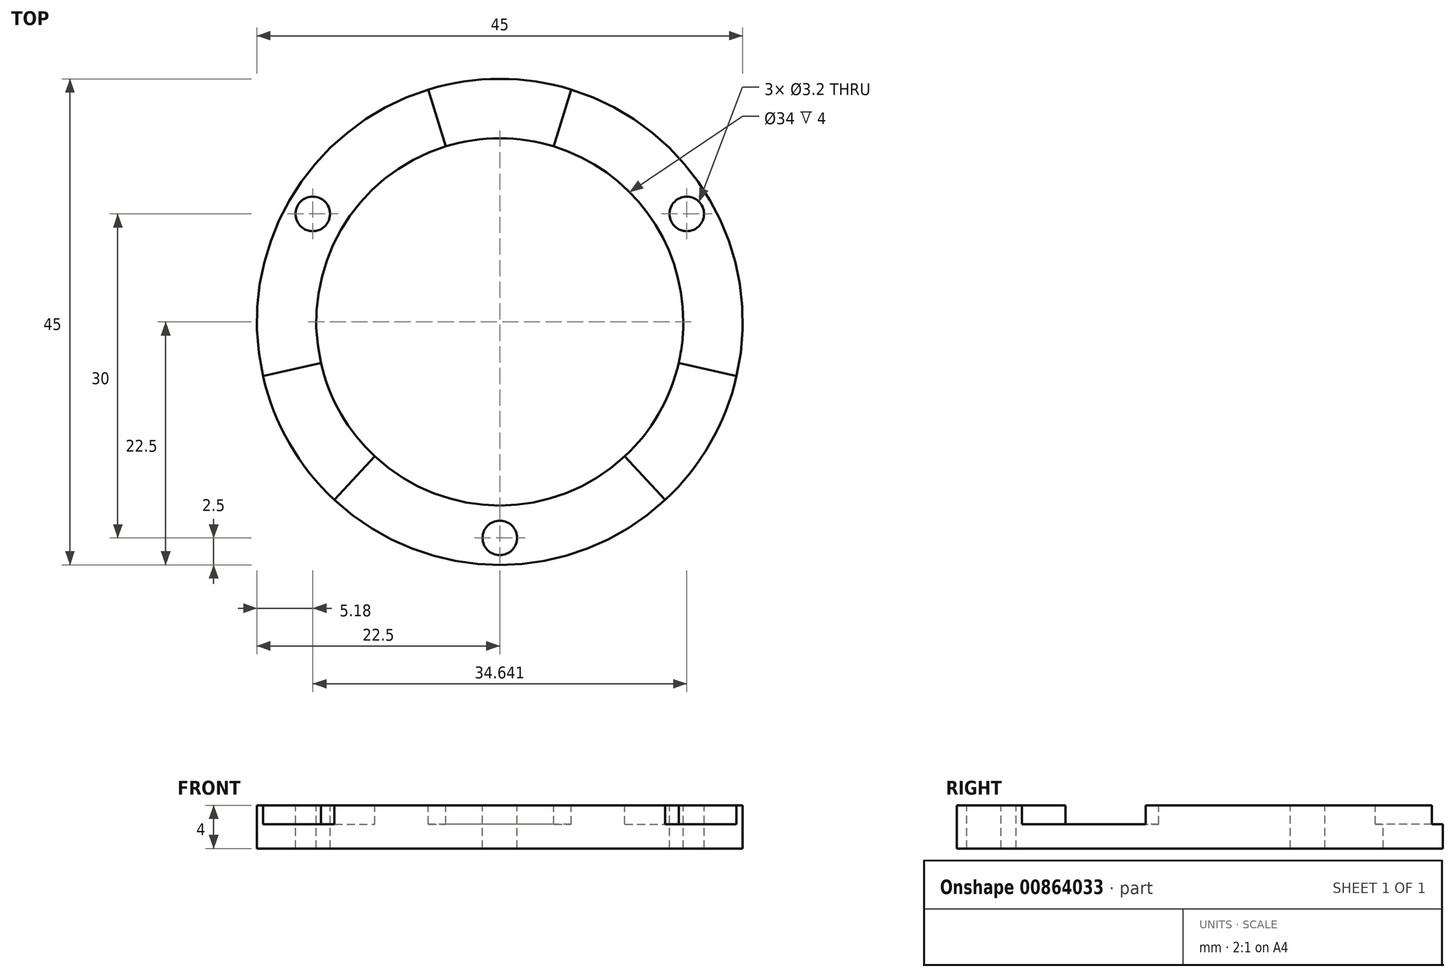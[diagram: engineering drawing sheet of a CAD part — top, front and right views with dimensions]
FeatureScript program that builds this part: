
annotation { "Feature Type Name" : "Feature", "Feature Type Description" : "" }
export const myFeature = defineFeature(function(context is Context, id is Id, definition is map)
    precondition{}
    {
        {
            var Q0;
            Q0=qCreatedBy(makeId("Top.planeOp"),FACE);
            var sketch = newSketch(context, id + "F0", { "sketchPlane" : qUnion([Q0])});
            skCircle(sketch, "E0", {"center": v(0, 0) * mm, "radius": 22.5 * mm});
            skSolve(sketch);
        }
        {
            var Q0;
            Q0 = qSketchRegion(id + "F0", true);
            extrude(context, id + "F1", {"entities" : qUnion([Q0]), "depth" : 4 * mm, "offsetDistance" : 25 * mm});
        }
        {
            var Q0;
            Q0=makeQuery(id+"F1.opExtrude","CAP_FACE",FACE,{"disambiguationData":[OSD([sQuery(id+"F0.wireOp",EDGE,"E0")])],"isStart":false});
            var sketch = newSketch(context, id + "F2", { "sketchPlane" : qUnion([Q0])});
            skCircle(sketch, "E1", {"center": v(0, 0) * mm, "radius": 17 * mm});
            skSolve(sketch);
        }
        {
            var Q0;
            Q0 = qSketchRegion(id + "F2", true);
            extrude(context, id + "F3", {"entities" : qUnion([Q0]), "operationType" : NewBodyOperationType.REMOVE, "oppositeDirection" : true, "depth" : 4 * mm, "offsetDistance" : 25 * mm});
        }
        {
            var Q0;
            Q0=makeQuery(id+"F1.opExtrude","CAP_FACE",FACE,{"disambiguationData":[OSD([sQuery(id+"F0.wireOp",EDGE,"E0")])],"isStart":false});
            var sketch = newSketch(context, id + "F4", { "sketchPlane" : qUnion([Q0])});
            skLineSegment(sketch, "E2", {"start": v(0, 0) * mm, "end": v(-6.62, 21.5) * mm, "construction": true});
            skLineSegment(sketch, "E3", {"start": v(0, 0) * mm, "end": v(6.62, 21.5) * mm, "construction": true});
            skLineSegment(sketch, "E4", {"start": v(-5, 16.25) * mm, "end": v(5, 16.25) * mm, "construction": true});
            skArc(sketch, "E5", {"start": v(-5, 16.25) * mm, "mid": v(0, 17) * mm, "end": v(5, 16.25) * mm});
            skArc(sketch, "E6", {"start": v(6.62, 21.5) * mm, "mid": v(0, 22.5) * mm, "end": v(-6.62, 21.5) * mm});
            skLineSegment(sketch, "E7", {"start": v(-6.62, 21.5) * mm, "end": v(-5, 16.25) * mm});
            skLineSegment(sketch, "E8", {"start": v(5, 16.25) * mm, "end": v(6.62, 21.5) * mm});
            skArc(sketch, "E9.1.0", {"start": v(-21.93, -5.02) * mm, "mid": v(-19.49, -11.25) * mm, "end": v(-15.31, -16.48) * mm});
            skArc(sketch, "E9.2.0", {"start": v(15.31, -16.48) * mm, "mid": v(19.49, -11.25) * mm, "end": v(21.93, -5.02) * mm});
            skArc(sketch, "E10.1.0", {"start": v(-11.57, -12.45) * mm, "mid": v(-14.72, -8.5) * mm, "end": v(-16.57, -3.8) * mm});
            skArc(sketch, "E10.2.0", {"start": v(16.57, -3.8) * mm, "mid": v(14.72, -8.5) * mm, "end": v(11.57, -12.45) * mm});
            skLineSegment(sketch, "E11.1.0", {"start": v(0, 0) * mm, "end": v(-21.93, -5.02) * mm, "construction": true});
            skLineSegment(sketch, "E11.2.0", {"start": v(0, 0) * mm, "end": v(15.31, -16.48) * mm, "construction": true});
            skLineSegment(sketch, "E12.1.0", {"start": v(0, 0) * mm, "end": v(-15.31, -16.48) * mm, "construction": true});
            skLineSegment(sketch, "E12.2.0", {"start": v(0, 0) * mm, "end": v(21.93, -5.02) * mm, "construction": true});
            skLineSegment(sketch, "E13", {"start": v(-21.93, -5.02) * mm, "end": v(-16.57, -3.8) * mm});
            skLineSegment(sketch, "E14", {"start": v(-15.31, -16.48) * mm, "end": v(-11.57, -12.45) * mm});
            skLineSegment(sketch, "E15", {"start": v(11.57, -12.45) * mm, "end": v(15.31, -16.48) * mm});
            skLineSegment(sketch, "E16", {"start": v(16.57, -3.8) * mm, "end": v(21.93, -5.02) * mm});
            skSolve(sketch);
        }
        {
            var Q0;
            Q0 = qSketchRegion(id + "F4", true);
            extrude(context, id + "F5", {"entities" : qUnion([Q0]), "operationType" : NewBodyOperationType.REMOVE, "oppositeDirection" : true, "depth" : 1.75 * mm, "offsetDistance" : 25 * mm});
        }
        {
            var Q0;
            {var subQ0=sQuery(id+"F0.wireOp",EDGE,"E0");Q0=makeQuery(id+"F5.boolean.opBoolean","SPLIT",FACE,{"disambiguationData":[TD([makeQuery(id+"F5.opExtrude","SWEPT_FACE",FACE,{"disambiguationData":[OSD([sQuery(id+"F4.wireOp",EDGE,"E7")])]})])],"derivedFrom":makeQuery(id+"F1.opExtrude","CAP_FACE",FACE,{"disambiguationData":[OSD([subQ0])],"isStart":false})});}
            var sketch = newSketch(context, id + "F6", { "sketchPlane" : qUnion([Q0])});
            skCircle(sketch, "E17", {"center": v(0, -20) * mm, "radius": 1.6 * mm});
            skCircle(sketch, "E18.1.0", {"center": v(17.32, 10) * mm, "radius": 1.6 * mm});
            skCircle(sketch, "E18.2.0", {"center": v(-17.32, 10) * mm, "radius": 1.6 * mm});
            skPoint(sketch, "E18.center", {"position": v(0, 0) * mm});
            skSolve(sketch);
        }
        {
            var Q0;
            Q0 = qSketchRegion(id + "F6", true);
            extrude(context, id + "F7", {"entities" : qUnion([Q0]), "operationType" : NewBodyOperationType.REMOVE, "oppositeDirection" : true, "depth" : 4 * mm, "offsetDistance" : 25 * mm});
        }
    });
